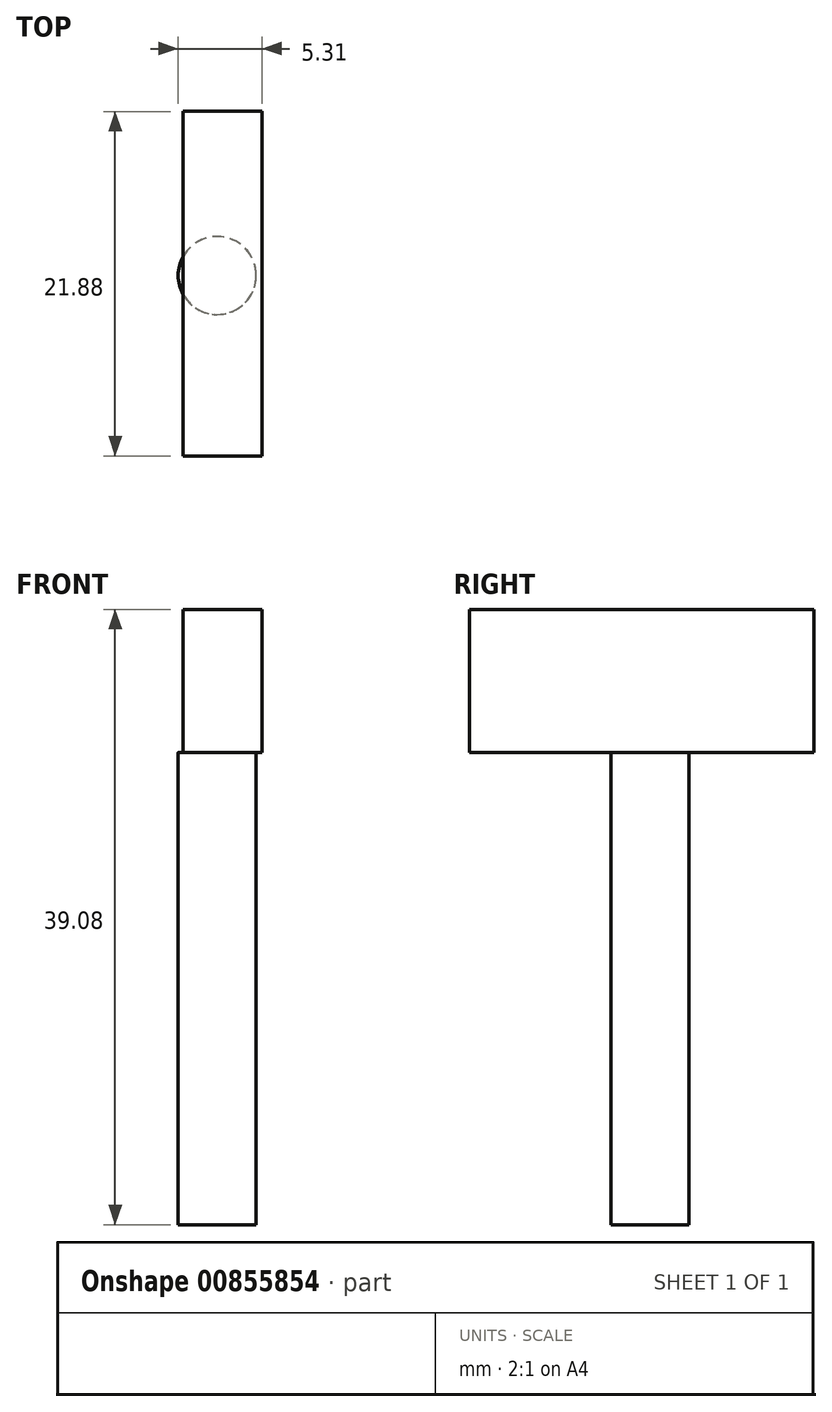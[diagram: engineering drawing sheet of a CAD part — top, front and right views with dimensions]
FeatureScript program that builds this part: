
annotation { "Feature Type Name" : "Feature", "Feature Type Description" : "" }
export const myFeature = defineFeature(function(context is Context, id is Id, definition is map)
    precondition{}
    {
        {
            var Q0;
            Q0=qCreatedBy(makeId("Right.planeOp"),FACE);
            var sketch = newSketch(context, id + "F0", { "sketchPlane" : qUnion([Q0])});
            skLineSegment(sketch, "E0.bottom", {"start": v(-66.78, 9.08) * mm, "end": v(-44.9, 9.08) * mm});
            skLineSegment(sketch, "E0.top", {"start": v(-66.78, 0) * mm, "end": v(-44.9, 0) * mm});
            skLineSegment(sketch, "E0.left", {"start": v(-66.78, 9.08) * mm, "end": v(-66.78, 0) * mm});
            skLineSegment(sketch, "E0.right", {"start": v(-44.9, 9.08) * mm, "end": v(-44.9, 0) * mm});
            skSolve(sketch);
        }
        {
            var Q0;
            Q0 = qSketchRegion(id + "F0", true);
            extrude(context, id + "F1", {"entities" : qUnion([Q0]), "depth" : 5 * mm, "offsetDistance" : 25 * mm});
        }
        {
            var Q0;
            Q0=qCreatedBy(makeId("Top.planeOp"),FACE);
            var sketch = newSketch(context, id + "F2", { "sketchPlane" : qUnion([Q0])});
            skCircle(sketch, "E1", {"center": v(2.17, -55.32) * mm, "radius": 2.48 * mm});
            skSolve(sketch);
        }
        {
            var Q0;
            Q0 = qSketchRegion(id + "F2", true);
            extrude(context, id + "F3", {"entities" : qUnion([Q0]), "operationType" : NewBodyOperationType.ADD, "oppositeDirection" : true, "depth" : 30 * mm, "offsetDistance" : 25 * mm});
        }
    });
